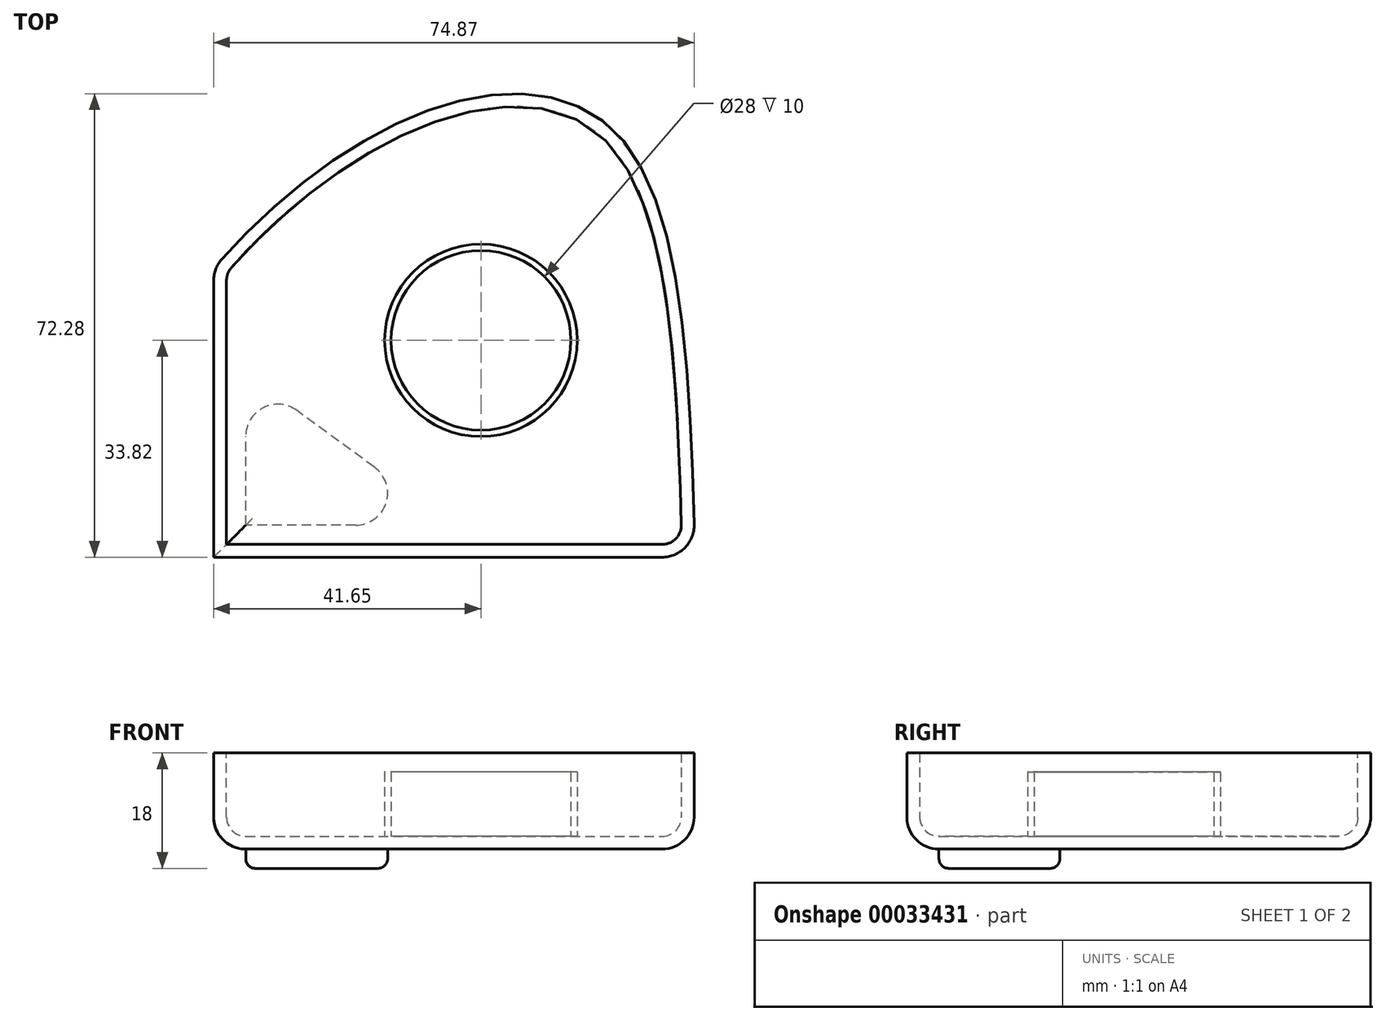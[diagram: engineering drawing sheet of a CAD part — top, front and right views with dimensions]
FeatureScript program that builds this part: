
annotation { "Feature Type Name" : "Feature", "Feature Type Description" : "" }
export const myFeature = defineFeature(function(context is Context, id is Id, definition is map)
    precondition{}
    {
        {
            var Q0;
            Q0=qCreatedBy(makeId("Top.planeOp"),FACE);
            var sketch = newSketch(context, id + "F0", { "sketchPlane" : qUnion([Q0])});
            skLineSegment(sketch, "E0", {"start": v(28.22, -33.82) * mm, "end": v(-41.65, -33.82) * mm});
            skLineSegment(sketch, "E1", {"start": v(-41.65, -33.82) * mm, "end": v(-41.65, 9.32) * mm});
            skFitSpline(sketch, "E2", {"points": [v(-41.65, 11.18) * mm, v(-5.07, 36.88) * mm, v(21.98, 31.35) * mm, v(33.35, -33.82) * mm], "startDerivative": vector(86.42, 102.25) * mm, "endDerivative": vector(4.92, -196.63) * mm});
            skArc(sketch, "E3.filletArc", {"start": v(28.22, -33.82) * mm, "mid": v(31.8, -32.3) * mm, "end": v(33.22, -28.68) * mm});
            skArc(sketch, "E4.filletArc", {"start": v(-40.4, 12.63) * mm, "mid": v(-41.32, 11.09) * mm, "end": v(-41.65, 9.32) * mm});
            skSolve(sketch);
        }
        {
            var Q0;
            Q0=makeQuery(id+"F0.imprint","IMPRINT",FACE,{"disambiguationData":[TD([[makeQuery(id+"F0.imprint","IMPRINT",EDGE,{"derivedFrom":sQuery(id+"F0.wireOp",EDGE,"E0")}),-1.0]])]});
            extrude(context, id + "F1", {"entities" : qUnion([Q0]), "depth" : 15 * mm});
        }
        {
            var Q0;
            Q0=makeQuery(id+"F1.opExtrude","CAP_EDGE",EDGE,{"disambiguationData":[OSD([sQuery(id+"F0.wireOp",EDGE,"E1")])],"isStart":true});
            fillet(context, id + "F2", {"entities" : qUnion([Q0]), "radius" : 5 * mm, "tangentPropagation" : true, "allowEdgeOverflow" : false});
        }
        {
            var Q0;
            Q0=makeQuery(id+"F1.opExtrude","CAP_FACE",FACE,{"disambiguationData":[OSD([sQuery(id+"F0.wireOp",EDGE,"E0"),sQuery(id+"F0.wireOp",EDGE,"E1"),sQuery(id+"F0.wireOp",EDGE,"E2"),sQuery(id+"F0.wireOp",EDGE,"E3.filletArc"),sQuery(id+"F0.wireOp",EDGE,"E4.filletArc")])],"isStart":false});
            shell(context, id + "F3", {"entities" : qUnion([Q0]), "thickness" : 2 * mm});
        }
        {
            var Q0;
            Q0=makeQuery(id+"F3.opShell","OFFSET_FACE",FACE,{"disambiguationData":[OSD([sQuery(id+"F0.wireOp",EDGE,"E0"),sQuery(id+"F0.wireOp",EDGE,"E1"),sQuery(id+"F0.wireOp",EDGE,"E2"),sQuery(id+"F0.wireOp",EDGE,"E3.filletArc"),sQuery(id+"F0.wireOp",EDGE,"E4.filletArc")])]});
            var sketch = newSketch(context, id + "F4", { "sketchPlane" : qUnion([Q0])});
            skCircle(sketch, "E5", {"center": v(0, 0) * mm, "radius": 15 * mm});
            skCircle(sketch, "E6", {"center": v(0, 0) * mm, "radius": 14 * mm});
            skSolve(sketch);
        }
        {
            var Q0;
            Q0=makeQuery(id+"F4.imprint","IMPRINT",FACE,{"disambiguationData":[TD([[makeQuery(id+"F4.imprint","IMPRINT",EDGE,{"derivedFrom":sQuery(id+"F4.wireOp",EDGE,"E5")}),1.0]])]});
            extrude(context, id + "F5", {"entities" : qUnion([Q0]), "operationType" : NewBodyOperationType.ADD, "depth" : 10 * mm});
        }
        {
            var Q0;
            Q0=makeQuery(id+"F1.opExtrude","CAP_FACE",FACE,{"disambiguationData":[OSD([sQuery(id+"F0.wireOp",EDGE,"E0"),sQuery(id+"F0.wireOp",EDGE,"E1"),sQuery(id+"F0.wireOp",EDGE,"E2"),sQuery(id+"F0.wireOp",EDGE,"E3.filletArc"),sQuery(id+"F0.wireOp",EDGE,"E4.filletArc")])],"isStart":true});
            var sketch = newSketch(context, id + "F6", { "sketchPlane" : qUnion([Q0])});
            skLineSegment(sketch, "E7", {"start": v(-36.65, 28.82) * mm, "end": v(-19.53, 28.82) * mm});
            skLineSegment(sketch, "E8", {"start": v(-16.59, 19.78) * mm, "end": v(-28.7, 10.93) * mm});
            skLineSegment(sketch, "E9", {"start": v(-36.65, 14.97) * mm, "end": v(-36.65, 28.82) * mm});
            skPoint(sketch, "E10.visualSharp", {"position": v(-36.65, 5.13) * mm});
            skArc(sketch, "E10.filletArc", {"start": v(-36.65, 14.97) * mm, "mid": v(-33.91, 10.51) * mm, "end": v(-28.7, 10.93) * mm});
            skPoint(sketch, "E11.visualSharp", {"position": v(-4.21, 28.82) * mm});
            skArc(sketch, "E11.filletArc", {"start": v(-16.59, 19.78) * mm, "mid": v(-14.78, 25.37) * mm, "end": v(-19.53, 28.82) * mm});
            skSolve(sketch);
        }
        {
            var Q0;
            Q0=makeQuery(id+"F6.imprint","IMPRINT",FACE,{"disambiguationData":[TD([[makeQuery(id+"F6.imprint","IMPRINT",EDGE,{"derivedFrom":sQuery(id+"F6.wireOp",EDGE,"E7")}),1.0]])]});
            extrude(context, id + "F7", {"entities" : qUnion([Q0]), "operationType" : NewBodyOperationType.ADD, "depth" : 3 * mm});
        }
        {
            var Q0;
            Q0=makeQuery(id+"F7.opExtrude","CAP_EDGE",EDGE,{"disambiguationData":[OSD([sQuery(id+"F6.wireOp",EDGE,"E7")])],"isStart":false});
            fillet(context, id + "F8", {"entities" : qUnion([Q0]), "radius" : 1.5 * mm, "tangentPropagation" : true, "allowEdgeOverflow" : false});
        }
    });
